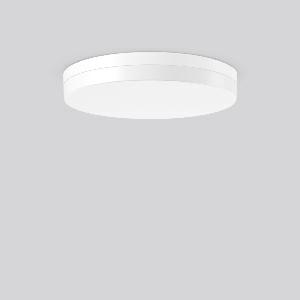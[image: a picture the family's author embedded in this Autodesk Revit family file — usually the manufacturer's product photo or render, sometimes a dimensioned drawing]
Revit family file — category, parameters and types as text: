
# Revit family: flat_slim_round_312634_002_5ffc
name_source: partatom
category: Lighting Fixtures
units: mm (PartAtom-declared; Revit-internal decimal feet)

## family parameters
Cut with Voids When Loaded = No
Host = Face
Light Source = No
Part Type = Normal
Room Calculation Point = No
Round Connector Dimension = Use Diameter
Shared = No

## types (1)
- MultiLumen 1 830 (1 x LED Modul 830, 3450 lm, 3000)
    Apparent Load = 26 VA
    CIE Flux Codes = 40 71 90 84 100
    Color Rendering = 80
    Color Temperature = 3000
    Default Elevation = 1800 mm
    Height = 70 mm
    Lamp = 1 x LED Modul 830
    Lamp Light Flux = 3450 lm
    Lamp count = 1
    Length = 480 mm
    Lifetime = 50000 h
    Luminous efficacy = 133 lm/W
    Manufacturer = RZB
    ModVariant = No
    Model = 312634.002
    Mounting Place = Ceiling
    Mounting Type = Surface mounted
    Number of Poles = 1
    OnlyDefault = Yes
    Power Factor = 1
    Product Name = FLAT SLIM round
    Product group = Surface mounted ceiling and wall luminaires
    ProductGroupID = 305
    Protection Class = Protection class I
    Protection Degree = Degree of protection
    RLX_Detail_Level = 1
    RLX_Emergency_Light_Flux = 0 lm
    RLX_Emergency_Type = 0
    RLX_Emergency_Type_DB = No
    RlxData = <blob elided: 21133 chars, md5=1fadf7d7>
    Socket = socket
    Standby Power = 0 W
    System Light Flux = 3450 lm
    System Power = 26 W
    Type Comments = MultiLumen 1 830
    Type Image = 312633.002.jpg
    URL = http://relux.com
    VarID = multilumen_1_830
    Voltage = 0 V
    Weight = 0.00 kg
    Width = 0 mm  [stored 0 ft]

note: [stored X ft] marks values corroborated as IEEE doubles in the binary element streams (Revit-internal decimal feet)

## geometry (parser evidence)
native form markers: Blend x4, Sweep x14
no freeform markers — native parametric forms only
